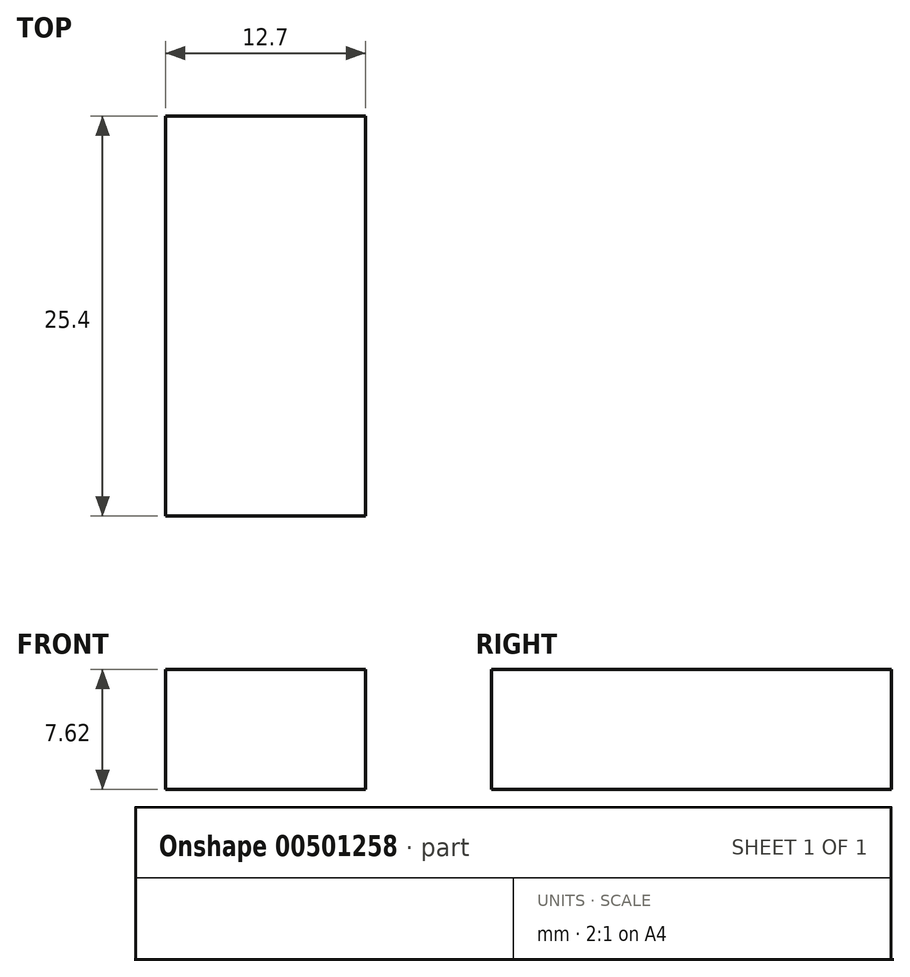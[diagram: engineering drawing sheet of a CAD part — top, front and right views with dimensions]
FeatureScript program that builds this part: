
annotation { "Feature Type Name" : "Feature", "Feature Type Description" : "" }
export const myFeature = defineFeature(function(context is Context, id is Id, definition is map)
    precondition{}
    {
        {
            var Q0;
            Q0=qCreatedBy(makeId("Top.planeOp"),FACE);
            var sketch = newSketch(context, id + "F0", { "sketchPlane" : qUnion([Q0])});
            skLineSegment(sketch, "E0.bottom", {"start": v(0, 0) * mm, "end": v(12.7, 0) * mm});
            skLineSegment(sketch, "E0.top", {"start": v(0, 25.4) * mm, "end": v(12.7, 25.4) * mm});
            skLineSegment(sketch, "E0.left", {"start": v(0, 0) * mm, "end": v(0, 25.4) * mm});
            skLineSegment(sketch, "E0.right", {"start": v(12.7, 0) * mm, "end": v(12.7, 25.4) * mm});
            skSolve(sketch);
        }
        {
            var Q0;
            Q0 = qSketchRegion(id + "F0", true);
            extrude(context, id + "F1", {"entities" : qUnion([Q0]), "depth" : 7.62 * mm});
        }
    });
